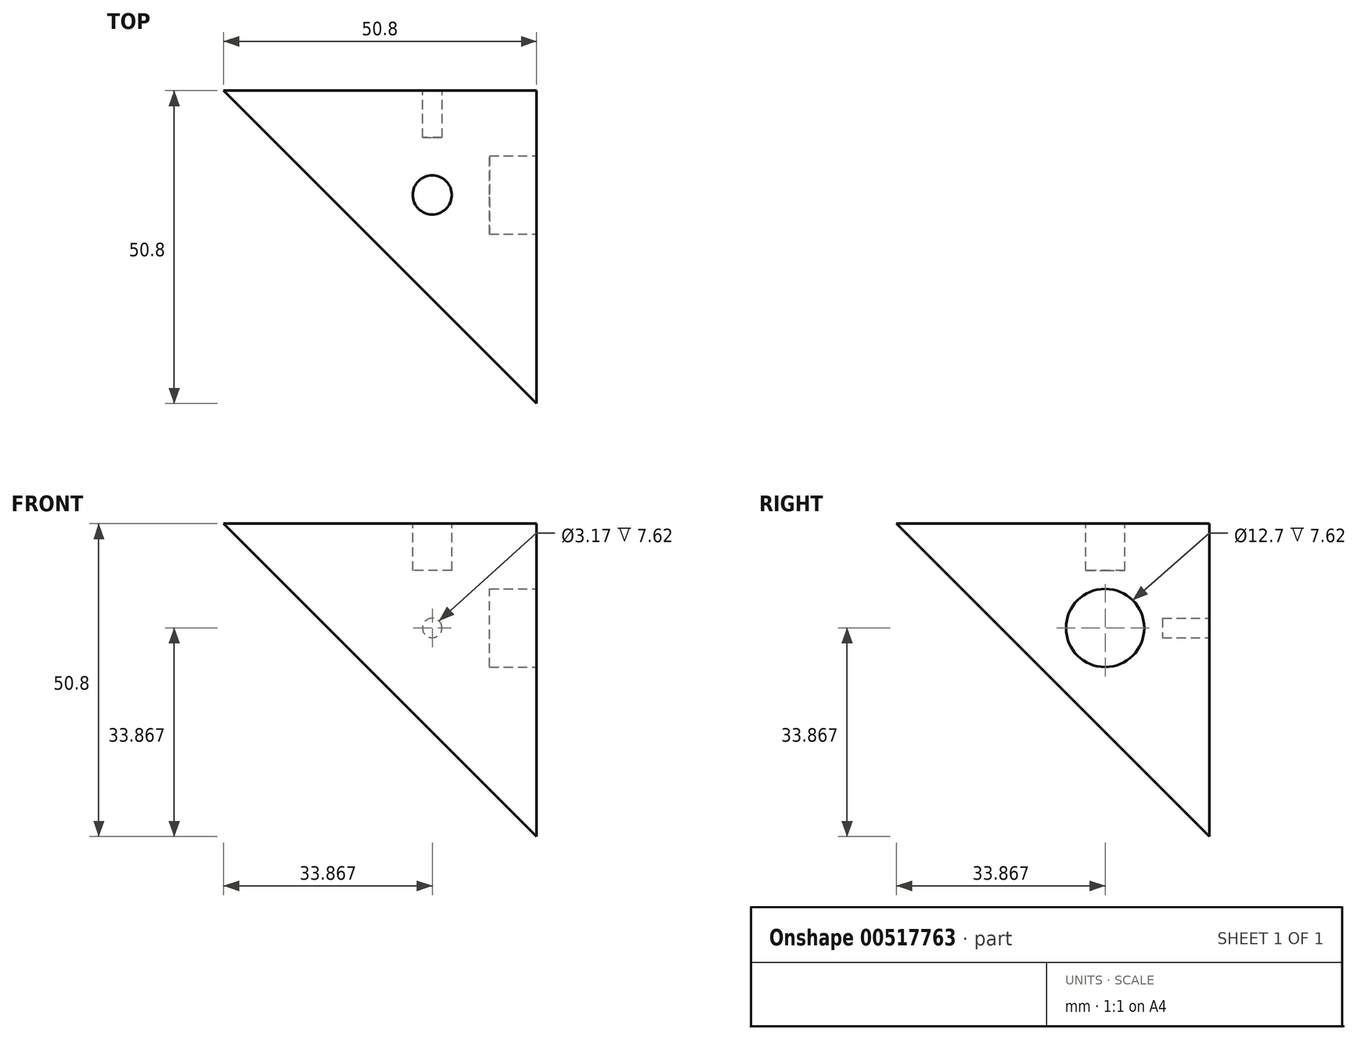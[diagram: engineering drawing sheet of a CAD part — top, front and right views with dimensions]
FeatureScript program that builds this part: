
annotation { "Feature Type Name" : "Feature", "Feature Type Description" : "" }
export const myFeature = defineFeature(function(context is Context, id is Id, definition is map)
    precondition{}
    {
        {
            var Q0;
            Q0=qCreatedBy(makeId("Top.planeOp"),FACE);
            var sketch = newSketch(context, id + "F0", { "sketchPlane" : qUnion([Q0])});
            skLineSegment(sketch, "E0.bottom", {"start": v(25.4, 25.4) * mm, "end": v(-25.4, 25.4) * mm});
            skLineSegment(sketch, "E0.top", {"start": v(25.4, -25.4) * mm, "end": v(-25.4, -25.4) * mm});
            skLineSegment(sketch, "E0.left", {"start": v(25.4, 25.4) * mm, "end": v(25.4, -25.4) * mm});
            skLineSegment(sketch, "E0.right", {"start": v(-25.4, 25.4) * mm, "end": v(-25.4, -25.4) * mm});
            skPoint(sketch, "E0.middle", {"position": v(0, 0) * mm});
            skSolve(sketch);
        }
        {
            var Q0;
            Q0=makeQuery(id+"F0.imprint","IMPRINT",FACE,{"disambiguationData":[TD([[makeQuery(id+"F0.imprint","IMPRINT",EDGE,{"derivedFrom":sQuery(id+"F0.wireOp",EDGE,"E0.bottom")}),1.0]])]});
            extrude(context, id + "F1", {"entities" : qUnion([Q0]), "depth" : 50.8 * mm, "offsetDistance" : 25.4 * mm});
        }
        {
            var Q0;
            Q0=makeQuery(id+"F1.opExtrude","CAP_VERTEX",VERTEX,{"disambiguationData":[OSD([sQuery(id+"F0.wireOp",EDGE,"E0.top"),sQuery(id+"F0.wireOp",EDGE,"E0.left")])],"isStart":false});
            var Q1;
            Q1=makeQuery(id+"F1.opExtrude","CAP_VERTEX",VERTEX,{"disambiguationData":[OSD([sQuery(id+"F0.wireOp",EDGE,"E0.bottom"),sQuery(id+"F0.wireOp",EDGE,"E0.left")])],"isStart":true});
            var Q2;
            Q2=makeQuery(id+"F1.opExtrude","CAP_VERTEX",VERTEX,{"disambiguationData":[OSD([sQuery(id+"F0.wireOp",EDGE,"E0.bottom"),sQuery(id+"F0.wireOp",EDGE,"E0.right")])],"isStart":false});
            cPlane(context, id + "F2", {"entities" : qUnion([Q0, Q1, Q2]), "cplaneType" : CPlaneType.THREE_POINT, "offset" : 25.4 * mm, "width" : 152.4 * mm, "height" : 152.4 * mm});
        }
        {
            var Q0;
            Q0=qCreatedBy(id+"F2.planeOp",FACE);
            var sketch = newSketch(context, id + "F3", { "sketchPlane" : qUnion([Q0])});
            skPoint(sketch, "E1.0", {"position": v(-51.85, 17.96) * mm});
            skPoint(sketch, "E1.1", {"position": v(10.37, -17.96) * mm});
            skPoint(sketch, "E1.2", {"position": v(10.37, 53.88) * mm});
            skPoint(sketch, "E2.0", {"position": v(-31.1, -17.96) * mm});
            skPoint(sketch, "E2.1", {"position": v(31.1, 17.96) * mm});
            skPoint(sketch, "E2.2", {"position": v(-31.1, 53.88) * mm});
            skLineSegment(sketch, "E3", {"start": v(-31.1, -17.96) * mm, "end": v(10.37, -17.96) * mm});
            skLineSegment(sketch, "E4", {"start": v(10.37, -17.96) * mm, "end": v(31.1, 17.96) * mm});
            skLineSegment(sketch, "E5", {"start": v(31.1, 17.96) * mm, "end": v(10.37, 53.88) * mm});
            skLineSegment(sketch, "E6", {"start": v(10.37, 53.88) * mm, "end": v(-31.1, 53.88) * mm});
            skLineSegment(sketch, "E7", {"start": v(-31.1, 53.88) * mm, "end": v(-51.85, 17.96) * mm});
            skLineSegment(sketch, "E8", {"start": v(-51.85, 17.96) * mm, "end": v(-31.1, -17.96) * mm});
            skSolve(sketch);
        }
        {
            var Q0;
            Q0 = qSketchRegion(id + "F3", true);
            extrude(context, id + "F4", {"entities" : qUnion([Q0]), "operationType" : NewBodyOperationType.REMOVE, "endBound" : BoundingType.THROUGH_ALL, "depth" : 25.4 * mm, "offsetDistance" : 25.4 * mm});
        }
        {
            var Q0;
            Q0=makeQuery(id+"F1.opExtrude","SWEPT_FACE",FACE,{"disambiguationData":[OSD([sQuery(id+"F0.wireOp",EDGE,"E0.left")])]});
            var sketch = newSketch(context, id + "F5", { "sketchPlane" : qUnion([Q0])});
            skLineSegment(sketch, "E9", {"start": v(25.4, 25.4) * mm, "end": v(-25.4, 50.8) * mm, "construction": true});
            skLineSegment(sketch, "E10", {"start": v(0, 50.8) * mm, "end": v(25.4, 0) * mm, "construction": true});
            skLineSegment(sketch, "E11", {"start": v(0, 25.4) * mm, "end": v(25.4, 50.8) * mm, "construction": true});
            skPoint(sketch, "E12", {"position": v(8.47, 33.87) * mm});
            skCircle(sketch, "E13", {"center": v(8.47, 33.87) * mm, "radius": 6.35 * mm});
            skSolve(sketch);
        }
        {
            var Q0;
            Q0=makeQuery(id+"F1.opExtrude","CAP_FACE",FACE,{"disambiguationData":[OSD([sQuery(id+"F0.wireOp",EDGE,"E0.bottom"),sQuery(id+"F0.wireOp",EDGE,"E0.top"),sQuery(id+"F0.wireOp",EDGE,"E0.left"),sQuery(id+"F0.wireOp",EDGE,"E0.right")])],"isStart":false});
            var sketch = newSketch(context, id + "F6", { "sketchPlane" : qUnion([Q0])});
            skLineSegment(sketch, "E14", {"start": v(0, 0) * mm, "end": v(25.4, 25.4) * mm, "construction": true});
            skLineSegment(sketch, "E15", {"start": v(25.4, 0) * mm, "end": v(-25.4, 25.4) * mm, "construction": true});
            skLineSegment(sketch, "E16", {"start": v(0, 25.4) * mm, "end": v(25.4, -25.4) * mm, "construction": true});
            skPoint(sketch, "E17", {"position": v(8.47, 8.47) * mm});
            skCircle(sketch, "E18", {"center": v(8.47, 8.47) * mm, "radius": 3.18 * mm});
            skSolve(sketch);
        }
        {
            var Q0;
            Q0=makeQuery(id+"F1.opExtrude","SWEPT_FACE",FACE,{"disambiguationData":[OSD([sQuery(id+"F0.wireOp",EDGE,"E0.bottom")])]});
            var sketch = newSketch(context, id + "F7", { "sketchPlane" : qUnion([Q0])});
            skLineSegment(sketch, "E19", {"start": v(0, 25.4) * mm, "end": v(-25.4, 50.8) * mm, "construction": true});
            skLineSegment(sketch, "E20", {"start": v(0, 50.8) * mm, "end": v(-25.4, 0) * mm, "construction": true});
            skLineSegment(sketch, "E21", {"start": v(-25.4, 25.4) * mm, "end": v(25.4, 50.8) * mm, "construction": true});
            skPoint(sketch, "E22", {"position": v(-8.47, 33.87) * mm});
            skCircle(sketch, "E23", {"center": v(-8.47, 33.87) * mm, "radius": 1.59 * mm});
            skSolve(sketch);
        }
        {
            var Q0;
            Q0 = qSketchRegion(id + "F5", true);
            extrude(context, id + "F8", {"entities" : qUnion([Q0]), "operationType" : NewBodyOperationType.REMOVE, "oppositeDirection" : true, "depth" : 7.62 * mm, "offsetDistance" : 25.4 * mm});
        }
        {
            var Q0;
            Q0 = qSketchRegion(id + "F6", true);
            extrude(context, id + "F9", {"entities" : qUnion([Q0]), "operationType" : NewBodyOperationType.REMOVE, "oppositeDirection" : true, "depth" : 7.62 * mm, "offsetDistance" : 25.4 * mm});
        }
        {
            var Q0;
            Q0 = qSketchRegion(id + "F7", true);
            extrude(context, id + "F10", {"entities" : qUnion([Q0]), "operationType" : NewBodyOperationType.REMOVE, "oppositeDirection" : true, "depth" : 7.62 * mm, "offsetDistance" : 25.4 * mm});
        }
        {
            var Q0;
            Q0=qCreatedBy(id+"F2.planeOp",FACE);
            var sketch = newSketch(context, id + "F11", { "sketchPlane" : qUnion([Q0])});
            skPoint(sketch, "E24.0", {"position": v(10.37, 53.88) * mm});
            skPoint(sketch, "E24.1", {"position": v(-20.74, 0) * mm});
            skLineSegment(sketch, "E25", {"start": v(10.37, 53.88) * mm, "end": v(-20.74, 0) * mm, "construction": true});
            skSolve(sketch);
        }
        {
            var Q0;
            Q0=makeQuery(id+"F1.opExtrude","SWEPT_FACE",FACE,{"disambiguationData":[OSD([sQuery(id+"F0.wireOp",EDGE,"E0.bottom")])]});
            var sketch = newSketch(context, id + "F12", { "sketchPlane" : qUnion([Q0])});
            skPoint(sketch, "E26.0", {"position": v(-25.4, 50.8) * mm});
            skPoint(sketch, "E26.1", {"position": v(0, 25.4) * mm});
            skLineSegment(sketch, "E27", {"start": v(-25.4, 50.8) * mm, "end": v(0, 25.4) * mm, "construction": true});
            skSolve(sketch);
        }
        {
            var Q0;
            Q0=sQuery(id+"F12.wireOp",VERTEX,"E26.0");
            var Q1;
            Q1=sQuery(id+"F11.wireOp",VERTEX,"E24.1");
            var Q2;
            Q2=sQuery(id+"F11.wireOp",VERTEX,"E24.0");
            cPlane(context, id + "F13", {"entities" : qUnion([Q0, Q1, Q2]), "cplaneType" : CPlaneType.THREE_POINT, "offset" : 25.4 * mm, "width" : 152.4 * mm, "height" : 152.4 * mm});
        }
    });
